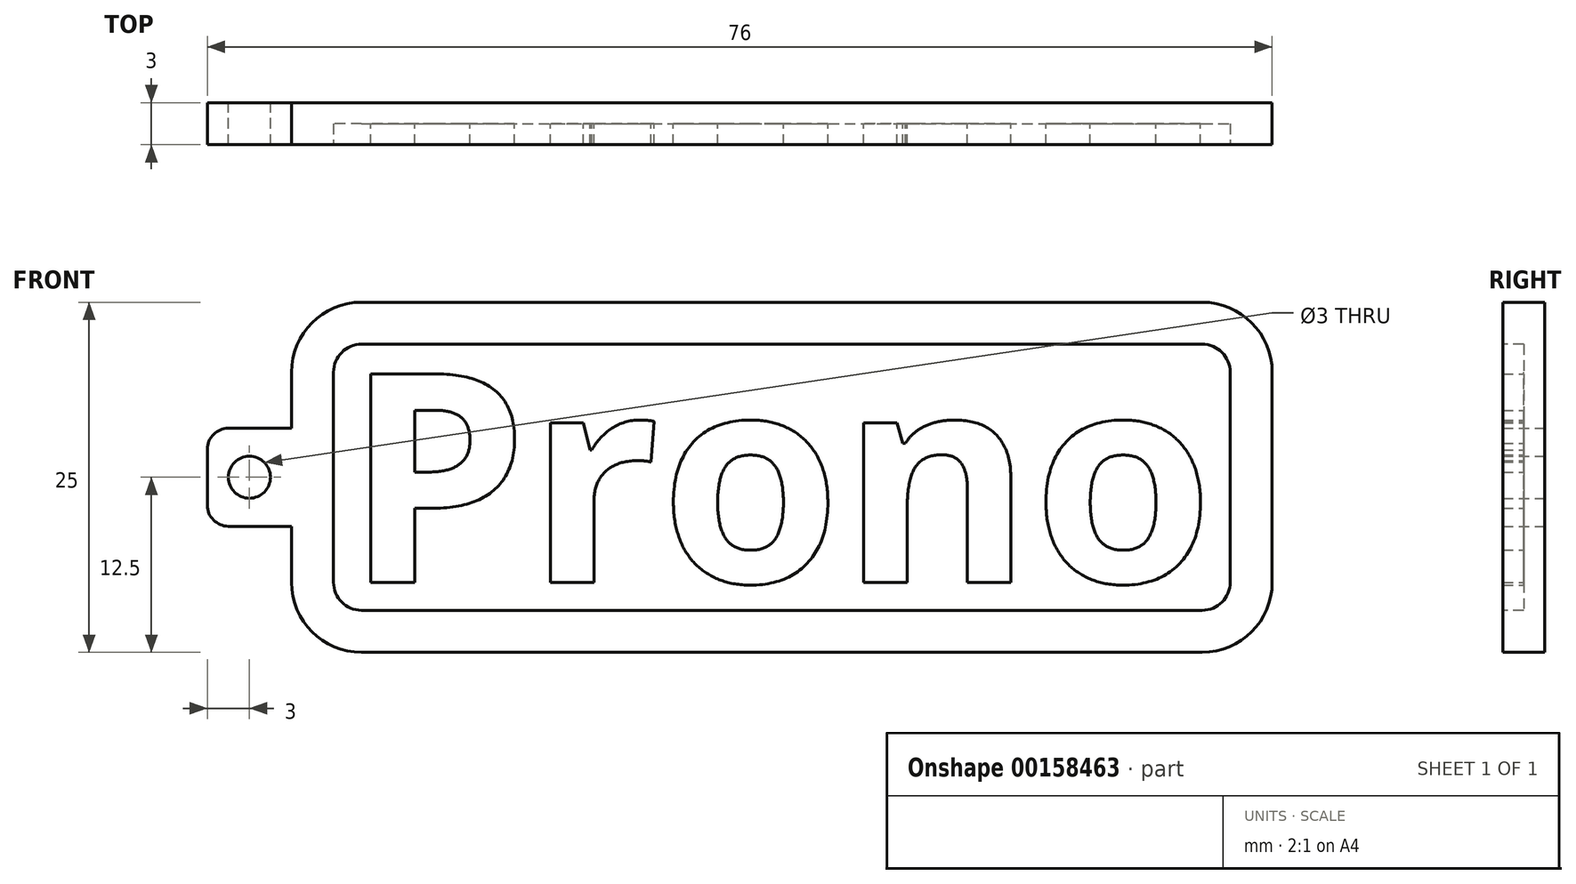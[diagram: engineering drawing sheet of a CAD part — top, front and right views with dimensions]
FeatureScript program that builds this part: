
annotation { "Feature Type Name" : "Feature", "Feature Type Description" : "" }
export const myFeature = defineFeature(function(context is Context, id is Id, definition is map)
    precondition{}
    {
        {
            var Q0;
            Q0=qCreatedBy(makeId("Front.planeOp"),FACE);
            var sketch = newSketch(context, id + "F0", { "sketchPlane" : qUnion([Q0])});
            skLineSegment(sketch, "E0.bottom", {"start": v(-35, -12.5) * mm, "end": v(35, -12.5) * mm});
            skLineSegment(sketch, "E0.top", {"start": v(-35, 12.5) * mm, "end": v(35, 12.5) * mm});
            skLineSegment(sketch, "E0.left", {"start": v(-35, -12.5) * mm, "end": v(-35, 12.5) * mm});
            skLineSegment(sketch, "E0.right", {"start": v(35, -12.5) * mm, "end": v(35, 12.5) * mm});
            skPoint(sketch, "E0.middle", {"position": v(0, 0) * mm});
            skSolve(sketch);
        }
        {
            var Q0;
            Q0=makeQuery(id+"F0.imprint","IMPRINT",FACE,{"disambiguationData":[TD([[makeQuery(id+"F0.imprint","IMPRINT",EDGE,{"derivedFrom":sQuery(id+"F0.wireOp",EDGE,"E0.bottom")}),1.0]])]});
            extrude(context, id + "F1", {"entities" : qUnion([Q0]), "oppositeDirection" : true, "depth" : 3 * mm});
        }
        {
            var Q0;
            Q0=makeQuery(id+"F1.opExtrude","SWEPT_EDGE",EDGE,{"disambiguationData":[OSD([sQuery(id+"F0.wireOp",EDGE,"E0.top"),sQuery(id+"F0.wireOp",EDGE,"E0.left")])]});
            var Q1;
            Q1=makeQuery(id+"F1.opExtrude","SWEPT_EDGE",EDGE,{"disambiguationData":[OSD([sQuery(id+"F0.wireOp",EDGE,"E0.top"),sQuery(id+"F0.wireOp",EDGE,"E0.right")])]});
            var Q2;
            Q2=makeQuery(id+"F1.opExtrude","SWEPT_EDGE",EDGE,{"disambiguationData":[OSD([sQuery(id+"F0.wireOp",EDGE,"E0.bottom"),sQuery(id+"F0.wireOp",EDGE,"E0.right")])]});
            var Q3;
            Q3=makeQuery(id+"F1.opExtrude","SWEPT_EDGE",EDGE,{"disambiguationData":[OSD([sQuery(id+"F0.wireOp",EDGE,"E0.bottom"),sQuery(id+"F0.wireOp",EDGE,"E0.left")])]});
            fillet(context, id + "F2", {"entities" : qUnion([Q0, Q1, Q2, Q3]), "radius" : 5 * mm, "tangentPropagation" : true, "allowEdgeOverflow" : false});
        }
        {
            var Q0;
            Q0=makeQuery(id+"F1.opExtrude","CAP_FACE",FACE,{"disambiguationData":[OSD([sQuery(id+"F0.wireOp",EDGE,"E0.bottom"),sQuery(id+"F0.wireOp",EDGE,"E0.top"),sQuery(id+"F0.wireOp",EDGE,"E0.left"),sQuery(id+"F0.wireOp",EDGE,"E0.right")])],"isStart":true});
            var sketch = newSketch(context, id + "F3", { "sketchPlane" : qUnion([Q0])});
            skLineSegment(sketch, "E1.0", {"start": v(-30, 9.5) * mm, "end": v(30, 9.5) * mm});
            skArc(sketch, "E1.1", {"start": v(32, 7.5) * mm, "mid": v(31.41, 8.91) * mm, "end": v(30, 9.5) * mm});
            skArc(sketch, "E1.2", {"start": v(-30, 9.5) * mm, "mid": v(-31.41, 8.91) * mm, "end": v(-32, 7.5) * mm});
            skLineSegment(sketch, "E1.3", {"start": v(32, -7.5) * mm, "end": v(32, 7.5) * mm});
            skLineSegment(sketch, "E1.4", {"start": v(-32, -7.5) * mm, "end": v(-32, 7.5) * mm});
            skArc(sketch, "E1.5", {"start": v(-32, -7.5) * mm, "mid": v(-31.41, -8.91) * mm, "end": v(-30, -9.5) * mm});
            skLineSegment(sketch, "E1.6", {"start": v(-30, -9.5) * mm, "end": v(30, -9.5) * mm});
            skArc(sketch, "E1.7", {"start": v(30, -9.5) * mm, "mid": v(31.41, -8.91) * mm, "end": v(32, -7.5) * mm});
            skSolve(sketch);
        }
        {
            var Q0;
            Q0=makeQuery(id+"F3.imprint","IMPRINT",FACE,{"disambiguationData":[TD([[makeQuery(id+"F3.imprint","IMPRINT",EDGE,{"derivedFrom":sQuery(id+"F3.wireOp",EDGE,"E1.0")}),-1.0]])]});
            extrude(context, id + "F4", {"entities" : qUnion([Q0]), "operationType" : NewBodyOperationType.REMOVE, "oppositeDirection" : true, "depth" : 1.5 * mm});
        }
        {
            var Q0;
            Q0=makeQuery(id+"F4.boolean.opBoolean","COPY",FACE,{"derivedFrom":makeQuery(id+"F4.opExtrude","CAP_FACE",FACE,{"disambiguationData":[OSD([sQuery(id+"F3.wireOp",EDGE,"E1.0"),sQuery(id+"F3.wireOp",EDGE,"E1.1"),sQuery(id+"F3.wireOp",EDGE,"E1.2"),sQuery(id+"F3.wireOp",EDGE,"E1.3"),sQuery(id+"F3.wireOp",EDGE,"E1.4"),sQuery(id+"F3.wireOp",EDGE,"E1.5"),sQuery(id+"F3.wireOp",EDGE,"E1.6"),sQuery(id+"F3.wireOp",EDGE,"E1.7")])],"isStart":false})});
            var sketch = newSketch(context, id + "F5", { "sketchPlane" : qUnion([Q0])});
            skText(sketch, "E2", { "text": "Prono", "fontName": "OpenSans-Bold.ttf"});
            skLineSegment(sketch, "E3", {"start": v(-31.22, 0) * mm, "end": v(31.22, 0) * mm, "construction": true});
            const initialGuessF5  = {"E2": [-0.03122, -0.0075, 1, 0, 0.015]};
            skSetInitialGuess(sketch, initialGuessF5);
            skSolve(sketch);
        }
        {
            var Q0;
            Q0=makeQuery(id+"F5.imprint","IMPRINT",FACE,{"disambiguationData":[TD([[makeQuery(id+"F5.imprint","IMPRINT",EDGE,{"derivedFrom":sQuery(id+"F5.wireOp",EDGE,"E2.sketch_text.stroke-0")}),-1.0]])]});
            var Q1;
            Q1=makeQuery(id+"F5.imprint","IMPRINT",FACE,{"disambiguationData":[TD([[makeQuery(id+"F5.imprint","IMPRINT",EDGE,{"derivedFrom":sQuery(id+"F5.wireOp",EDGE,"E2.sketch_text.stroke-16")}),-1.0]])]});
            var Q2;
            Q2=makeQuery(id+"F5.imprint","IMPRINT",FACE,{"disambiguationData":[TD([[makeQuery(id+"F5.imprint","IMPRINT",EDGE,{"derivedFrom":sQuery(id+"F5.wireOp",EDGE,"E2.sketch_text.stroke-29")}),-1.0]])]});
            var Q3;
            Q3=makeQuery(id+"F5.imprint","IMPRINT",FACE,{"disambiguationData":[TD([[makeQuery(id+"F5.imprint","IMPRINT",EDGE,{"derivedFrom":sQuery(id+"F5.wireOp",EDGE,"E2.sketch_text.stroke-47")}),-1.0]])]});
            var Q4;
            Q4=makeQuery(id+"F5.imprint","IMPRINT",FACE,{"disambiguationData":[TD([[makeQuery(id+"F5.imprint","IMPRINT",EDGE,{"derivedFrom":sQuery(id+"F5.wireOp",EDGE,"E2.sketch_text.stroke-64")}),-1.0]])]});
            extrude(context, id + "F6", {"entities" : qUnion([Q0, Q1, Q2, Q3, Q4]), "operationType" : NewBodyOperationType.ADD, "depth" : 1.5 * mm});
        }
        {
            var Q0;
            Q0=makeQuery(id+"F1.opExtrude","CAP_FACE",FACE,{"disambiguationData":[OSD([sQuery(id+"F0.wireOp",EDGE,"E0.bottom"),sQuery(id+"F0.wireOp",EDGE,"E0.top"),sQuery(id+"F0.wireOp",EDGE,"E0.left"),sQuery(id+"F0.wireOp",EDGE,"E0.right")])],"isStart":false});
            var sketch = newSketch(context, id + "F7", { "sketchPlane" : qUnion([Q0])});
            skLineSegment(sketch, "E4", {"start": v(0, 0) * mm, "end": v(62.43, 0) * mm, "construction": true});
            skLineSegment(sketch, "E5", {"start": v(35, 3.5) * mm, "end": v(41, 3.5) * mm});
            skLineSegment(sketch, "E6", {"start": v(41, 3.5) * mm, "end": v(41, 0) * mm});
            skLineSegment(sketch, "E7.MirrorCS", {"start": v(41, -3.5) * mm, "end": v(41, 0) * mm});
            skLineSegment(sketch, "E8.MirrorCS", {"start": v(35, -3.5) * mm, "end": v(41, -3.5) * mm});
            skLineSegment(sketch, "E9", {"start": v(38, 3.5) * mm, "end": v(38, -3.5) * mm, "construction": true});
            skCircle(sketch, "E10", {"center": v(38, 0) * mm, "radius": 1.5 * mm});
            skLineSegment(sketch, "E11", {"start": v(35, -3.5) * mm, "end": v(35, 3.5) * mm});
            skSolve(sketch);
        }
        {
            var Q0;
            Q0=makeQuery(id+"F7.imprint","IMPRINT",FACE,{"disambiguationData":[TD([[makeQuery(id+"F7.imprint","IMPRINT",EDGE,{"derivedFrom":sQuery(id+"F7.wireOp",EDGE,"E5")}),-1.0]])]});
            extrude(context, id + "F8", {"entities" : qUnion([Q0]), "operationType" : NewBodyOperationType.ADD, "oppositeDirection" : true, "depth" : 3 * mm});
        }
        {
            var Q0;
            Q0=makeQuery(id+"F8.opExtrude","SWEPT_EDGE",EDGE,{"disambiguationData":[OSD([sQuery(id+"F7.wireOp",EDGE,"E5"),sQuery(id+"F7.wireOp",EDGE,"E6")])]});
            var Q1;
            Q1=makeQuery(id+"F8.opExtrude","SWEPT_EDGE",EDGE,{"disambiguationData":[OSD([sQuery(id+"F7.wireOp",EDGE,"E7.MirrorCS"),sQuery(id+"F7.wireOp",EDGE,"E8.MirrorCS")])]});
            fillet(context, id + "F9", {"entities" : qUnion([Q0, Q1]), "radius" : 1.5 * mm, "tangentPropagation" : true, "allowEdgeOverflow" : false});
        }
    });
